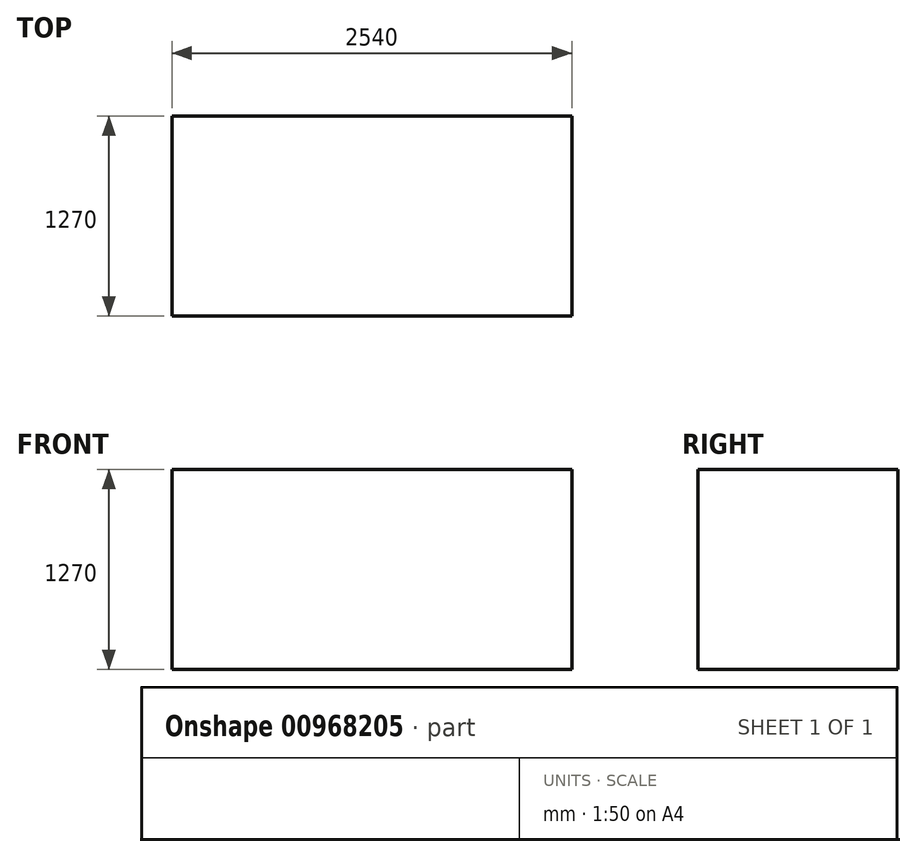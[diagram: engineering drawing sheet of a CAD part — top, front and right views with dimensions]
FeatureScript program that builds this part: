
annotation { "Feature Type Name" : "Feature", "Feature Type Description" : "" }
export const myFeature = defineFeature(function(context is Context, id is Id, definition is map)
    precondition{}
    {
        {
            var Q0;
            Q0=qCreatedBy(makeId("Front.planeOp"),FACE);
            var sketch = newSketch(context, id + "F0", { "sketchPlane" : qUnion([Q0])});
            skLineSegment(sketch, "E0.bottom", {"start": v(0, 0) * mm, "end": v(2540, 0) * mm});
            skLineSegment(sketch, "E0.top", {"start": v(0, 1270) * mm, "end": v(2540, 1270) * mm});
            skLineSegment(sketch, "E0.left", {"start": v(0, 0) * mm, "end": v(0, 1270) * mm});
            skLineSegment(sketch, "E0.right", {"start": v(2540, 0) * mm, "end": v(2540, 1270) * mm});
            skSolve(sketch);
        }
        {
            var Q0;
            Q0 = qSketchRegion(id + "F0", true);
            extrude(context, id + "F1", {"entities" : qUnion([Q0]), "depth" : 1270 * mm, "offsetDistance" : 25.4 * mm});
        }
    });
